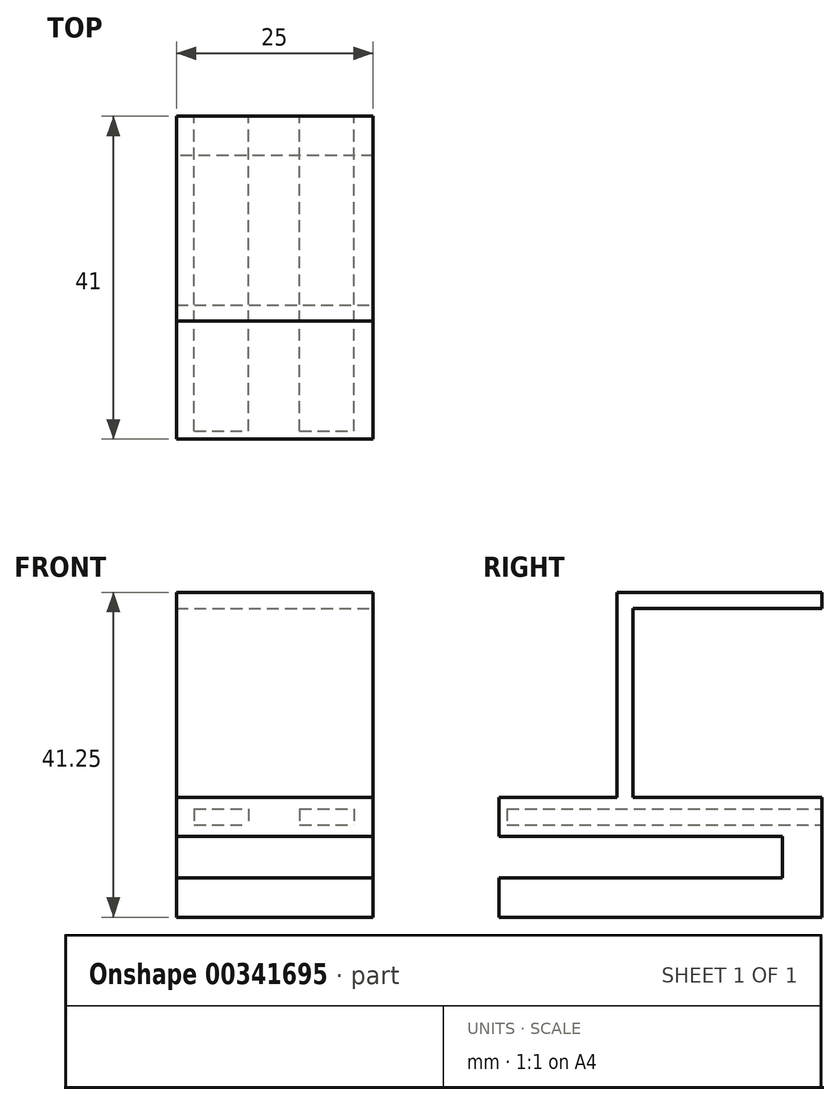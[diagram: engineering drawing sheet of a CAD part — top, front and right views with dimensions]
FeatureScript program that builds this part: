
annotation { "Feature Type Name" : "Feature", "Feature Type Description" : "" }
export const myFeature = defineFeature(function(context is Context, id is Id, definition is map)
    precondition{}
    {
        {
            var Q0;
            Q0=qCreatedBy(makeId("Front.planeOp"),FACE);
            var sketch = newSketch(context, id + "F0", { "sketchPlane" : qUnion([Q0])});
            skLineSegment(sketch, "E0.bottom", {"start": v(-12.15, 3.5) * mm, "end": v(12.85, 3.5) * mm});
            skLineSegment(sketch, "E0.top", {"start": v(-12.15, -1.5) * mm, "end": v(12.85, -1.5) * mm});
            skLineSegment(sketch, "E0.left", {"start": v(-12.15, 3.5) * mm, "end": v(-12.15, -1.5) * mm});
            skLineSegment(sketch, "E0.right", {"start": v(12.85, 3.5) * mm, "end": v(12.85, -1.5) * mm});
            skLineSegment(sketch, "E1.bottom", {"start": v(-9.9, 2) * mm, "end": v(-3, 2) * mm});
            skLineSegment(sketch, "E1.top", {"start": v(-9.9, 0) * mm, "end": v(-3, 0) * mm});
            skLineSegment(sketch, "E1.left", {"start": v(-9.9, 2) * mm, "end": v(-9.9, 0) * mm});
            skLineSegment(sketch, "E1.right", {"start": v(-3, 2) * mm, "end": v(-3, 0) * mm});
            skLineSegment(sketch, "E2.bottom", {"start": v(3.5, 2) * mm, "end": v(10.4, 2) * mm});
            skLineSegment(sketch, "E2.top", {"start": v(3.5, 0) * mm, "end": v(10.4, 0) * mm});
            skLineSegment(sketch, "E2.left", {"start": v(3.5, 2) * mm, "end": v(3.5, 0) * mm});
            skLineSegment(sketch, "E2.right", {"start": v(10.4, 2) * mm, "end": v(10.4, 0) * mm});
            skSolve(sketch);
        }
        {
            var Q0;
            Q0 = qSketchRegion(id + "F0", true);
            extrude(context, id + "F1", {"entities" : qUnion([Q0]), "depth" : 40 * mm});
        }
        {
            var Q0;
            Q0=makeQuery(id+"F1.opExtrude","CAP_FACE",FACE,{"disambiguationData":[OSD([sQuery(id+"F0.wireOp",EDGE,"E0.bottom"),sQuery(id+"F0.wireOp",EDGE,"E0.top"),sQuery(id+"F0.wireOp",EDGE,"E0.left"),sQuery(id+"F0.wireOp",EDGE,"E0.right"),sQuery(id+"F0.wireOp",EDGE,"E1.bottom"),sQuery(id+"F0.wireOp",EDGE,"E1.top"),sQuery(id+"F0.wireOp",EDGE,"E1.left"),sQuery(id+"F0.wireOp",EDGE,"E1.right"),sQuery(id+"F0.wireOp",EDGE,"E2.bottom"),sQuery(id+"F0.wireOp",EDGE,"E2.top"),sQuery(id+"F0.wireOp",EDGE,"E2.left"),sQuery(id+"F0.wireOp",EDGE,"E2.right")])],"isStart":false});
            var sketch = newSketch(context, id + "F2", { "sketchPlane" : qUnion([Q0])});
            skLineSegment(sketch, "E3.bottom", {"start": v(-12.15, 3.5) * mm, "end": v(12.85, 3.5) * mm});
            skLineSegment(sketch, "E3.top", {"start": v(-12.15, -1.5) * mm, "end": v(12.85, -1.5) * mm});
            skLineSegment(sketch, "E3.left", {"start": v(-12.15, 3.5) * mm, "end": v(-12.15, -1.5) * mm});
            skLineSegment(sketch, "E3.right", {"start": v(12.85, 3.5) * mm, "end": v(12.85, -1.5) * mm});
            skSolve(sketch);
        }
        {
            var Q0;
            Q0 = qSketchRegion(id + "F2", true);
            extrude(context, id + "F3", {"entities" : qUnion([Q0]), "operationType" : NewBodyOperationType.ADD, "depth" : 1 * mm});
        }
        {
            var Q0;
            Q0=makeQuery(id+"F3.boolean.opBoolean","MERGE",FACE,{"derivedFrom":[makeQuery(id+"F1.opExtrude","SWEPT_FACE",FACE,{"disambiguationData":[OSD([sQuery(id+"F0.wireOp",EDGE,"E0.top")])]}),makeQuery(id+"F3.opExtrude","SWEPT_FACE",FACE,{"disambiguationData":[OSD([sQuery(id+"F2.wireOp",EDGE,"E3.top")])]})]});
            var sketch = newSketch(context, id + "F4", { "sketchPlane" : qUnion([Q0])});
            skLineSegment(sketch, "E4.bottom", {"start": v(12.85, 0) * mm, "end": v(-12.15, 0) * mm});
            skLineSegment(sketch, "E4.top", {"start": v(12.85, 5) * mm, "end": v(-12.15, 5) * mm});
            skLineSegment(sketch, "E4.left", {"start": v(12.85, 0) * mm, "end": v(12.85, 5) * mm});
            skLineSegment(sketch, "E4.right", {"start": v(-12.15, 0) * mm, "end": v(-12.15, 5) * mm});
            skSolve(sketch);
        }
        {
            var Q0;
            Q0 = qSketchRegion(id + "F4", true);
            extrude(context, id + "F5", {"entities" : qUnion([Q0]), "operationType" : NewBodyOperationType.ADD, "depth" : 10.25 * mm});
        }
        {
            var Q0;
            Q0=makeQuery(id+"F5.opExtrude","SWEPT_FACE",FACE,{"disambiguationData":[OSD([sQuery(id+"F4.wireOp",EDGE,"E4.top")])]});
            var sketch = newSketch(context, id + "F6", { "sketchPlane" : qUnion([Q0])});
            skLineSegment(sketch, "E5.bottom", {"start": v(12.85, -11.75) * mm, "end": v(-12.15, -11.75) * mm});
            skLineSegment(sketch, "E5.top", {"start": v(12.85, -6.75) * mm, "end": v(-12.15, -6.75) * mm});
            skLineSegment(sketch, "E5.left", {"start": v(12.85, -11.75) * mm, "end": v(12.85, -6.75) * mm});
            skLineSegment(sketch, "E5.right", {"start": v(-12.15, -11.75) * mm, "end": v(-12.15, -6.75) * mm});
            skSolve(sketch);
        }
        {
            var Q0;
            Q0 = qSketchRegion(id + "F6", true);
            extrude(context, id + "F7", {"entities" : qUnion([Q0]), "operationType" : NewBodyOperationType.ADD, "depth" : 36 * mm});
        }
        {
            var Q0;
            Q0=makeQuery(id+"F3.boolean.opBoolean","MERGE",FACE,{"derivedFrom":[makeQuery(id+"F1.opExtrude","SWEPT_FACE",FACE,{"disambiguationData":[OSD([sQuery(id+"F0.wireOp",EDGE,"E0.bottom")])]}),makeQuery(id+"F3.opExtrude","SWEPT_FACE",FACE,{"disambiguationData":[OSD([sQuery(id+"F2.wireOp",EDGE,"E3.bottom")])]})]});
            var sketch = newSketch(context, id + "F8", { "sketchPlane" : qUnion([Q0])});
            skLineSegment(sketch, "E6.bottom", {"start": v(-12.15, -26) * mm, "end": v(12.85, -26) * mm});
            skLineSegment(sketch, "E6.top", {"start": v(-12.15, -24) * mm, "end": v(12.85, -24) * mm});
            skLineSegment(sketch, "E6.left", {"start": v(-12.15, -24) * mm, "end": v(-12.15, -26) * mm});
            skLineSegment(sketch, "E6.right", {"start": v(12.85, -24) * mm, "end": v(12.85, -26) * mm});
            skSolve(sketch);
        }
        {
            var Q0;
            Q0 = qSketchRegion(id + "F8", true);
            extrude(context, id + "F9", {"entities" : qUnion([Q0]), "operationType" : NewBodyOperationType.ADD, "depth" : 26 * mm});
        }
        {
            var Q0;
            Q0=makeQuery(id+"F9.opExtrude","SWEPT_FACE",FACE,{"disambiguationData":[OSD([sQuery(id+"F8.wireOp",EDGE,"E6.top")])]});
            var sketch = newSketch(context, id + "F10", { "sketchPlane" : qUnion([Q0])});
            skLineSegment(sketch, "E7.bottom", {"start": v(12.15, 29.5) * mm, "end": v(-12.85, 29.5) * mm});
            skLineSegment(sketch, "E7.top", {"start": v(12.15, 27.5) * mm, "end": v(-12.85, 27.5) * mm});
            skLineSegment(sketch, "E7.left", {"start": v(12.15, 29.5) * mm, "end": v(12.15, 27.5) * mm});
            skLineSegment(sketch, "E7.right", {"start": v(-12.85, 29.5) * mm, "end": v(-12.85, 27.5) * mm});
            skSolve(sketch);
        }
        {
            var Q0;
            Q0 = qSketchRegion(id + "F10", true);
            extrude(context, id + "F11", {"entities" : qUnion([Q0]), "operationType" : NewBodyOperationType.ADD, "depth" : 24 * mm});
        }
    });
